# Revit family: Emeco - 1 Inch Stool - Seat Material - Color - Aluminum Frame Finish
name_source: partatom
category: Furniture
revit_build: Autodesk Revit MEP 2014 (Build: 20140709_2115(x64)
units: mm (PartAtom-declared; Revit-internal decimal feet)

## types (20) — shared parameters
Assembly Code = E2020200
Description = Stool
Glide Material = Emeco-Glide-Plastic-Grey
Manufacturer = Emeco
URL = https://www.emeco.net
Upholster Material = Emeco-Upholester-Fabric

## per-type parameters (varying)
| type | Chair Frame Material | Fabric Visibility | Plastic Visibility | Plywood Material | Plywood Visibility | Seat Material_Fabric | Seat Material_Plastic_Blue | Seat Material_Plastic_Bordeaux | Seat Material_Plastic_Brown | Seat Material_Plastic_Dark Grey | Seat Material_Plastic_Green | Seat Material_Plastic_Light Grey | Seat Material_Plastic_Ochre Red | Seat Material_Plywood_Ash | Seat Material_Plywood_Walnut | Seat Type Selector |
| Reclaimed Polypropylene - Blue - Black Frame | Emeco-Frame-Metal-Aluminum-Black Powder Coated | No | Yes | Emeco-Seat-Plywood-Walnut | No | No | Yes | No | No | No | No | No | No | No | No | 9 |
| Reclaimed Polypropylene - Blue - Brushed Frame | Emeco-Frame-Metal-Aluminium-Brushed | No | Yes | Emeco-Seat-Plywood-Walnut | No | No | Yes | No | No | No | No | No | No | No | No | 9 |
| Reclaimed Polypropylene - Bordeaux - Black Frame | Emeco-Frame-Metal-Aluminum-Black Powder Coated | No | Yes | Emeco-Seat-Plywood-Walnut | No | No | No | Yes | No | No | No | No | No | No | No | 8 |
| Reclaimed Polypropylene - Bordeaux - Brushed Frame | Emeco-Frame-Metal-Aluminium-Brushed | No | Yes | Emeco-Seat-Plywood-Walnut | No | No | No | Yes | No | No | No | No | No | No | No | 8 |
| Reclaimed Polypropylene - Brown - Black Frame | Emeco-Frame-Metal-Aluminum-Black Powder Coated | No | Yes | Emeco-Seat-Plywood-Walnut | No | No | No | No | Yes | No | No | No | No | No | No | 7 |
| Reclaimed Polypropylene - Brown - Brushed Frame | Emeco-Frame-Metal-Aluminium-Brushed | No | Yes | Emeco-Seat-Plywood-Walnut | No | No | No | No | Yes | No | No | No | No | No | No | 7 |
| Reclaimed Polypropylene - Dark Grey - Black Frame | Emeco-Frame-Metal-Aluminum-Black Powder Coated | No | Yes | Emeco-Seat-Plywood-Walnut | No | No | No | No | No | Yes | No | No | No | No | No | 6 |
| Reclaimed Polypropylene - Dark Grey - Brushed Frame | Emeco-Frame-Metal-Aluminium-Brushed | No | Yes | Emeco-Seat-Plywood-Walnut | No | No | No | No | No | Yes | No | No | No | No | No | 6 |
| Reclaimed Polypropylene - Green - Black Frame | Emeco-Frame-Metal-Aluminum-Black Powder Coated | No | Yes | Emeco-Seat-Plywood-Walnut | No | No | No | No | No | No | Yes | No | No | No | No | 5 |
| Reclaimed Polypropylene - Green - Brushed Frame | Emeco-Frame-Metal-Aluminium-Brushed | No | Yes | Emeco-Seat-Plywood-Walnut | No | No | No | No | No | No | Yes | No | No | No | No | 5 |
| Reclaimed Polypropylene - Light Grey - Black Frame | Emeco-Frame-Metal-Aluminum-Black Powder Coated | No | Yes | Emeco-Seat-Plywood-Walnut | No | No | No | No | No | No | No | Yes | No | No | No | 4 |
| Reclaimed Polypropylene - Light Grey - Brushed Frame | Emeco-Frame-Metal-Aluminium-Brushed | No | Yes | Emeco-Seat-Plywood-Walnut | No | No | No | No | No | No | No | Yes | No | No | No | 4 |
| Reclaimed Polypropylene - Ochre Red - Black Frame | Emeco-Frame-Metal-Aluminum-Black Powder Coated | No | Yes | Emeco-Seat-Plywood-Walnut | No | No | No | No | No | No | No | No | Yes | No | No | 3 |
| Reclaimed Polypropylene - Ochre Red - Brushed Frame | Emeco-Frame-Metal-Aluminium-Brushed | No | Yes | Emeco-Seat-Plywood-Walnut | No | No | No | No | No | No | No | No | Yes | No | No | 3 |
| Upholstered - Grey Fabric - Black Frame | Emeco-Frame-Metal-Aluminum-Black Powder Coated | Yes | No | Emeco-Seat-Plywood-Walnut | No | Yes | No | No | No | No | No | No | No | No | No | 0 |
| Upholstered - Grey Fabric - Brushed Frame | Emeco-Frame-Metal-Aluminium-Brushed | Yes | No | Emeco-Seat-Plywood-Walnut | No | Yes | No | No | No | No | No | No | No | No | No | 0 |
| Wood - Ash - Black Frame | Emeco-Frame-Metal-Aluminum-Black Powder Coated | No | No | Emeco-Seat-Plywood-Ash | Yes | No | No | No | No | No | No | No | No | Yes | No | 2 |
| Wood - Ash - Brushed Frame | Emeco-Frame-Metal-Aluminium-Brushed | No | No | Emeco-Seat-Plywood-Ash | Yes | No | No | No | No | No | No | No | No | Yes | No | 2 |
| Wood - Walnut - Black Frame | Emeco-Frame-Metal-Aluminum-Black Powder Coated | No | No | Emeco-Seat-Plywood-Walnut | Yes | No | No | No | No | No | No | No | No | No | Yes | 1 |
| Wood - Walnut - Brushed Frame | Emeco-Frame-Metal-Aluminium-Brushed | No | No | Emeco-Seat-Plywood-Walnut | Yes | No | No | No | No | No | No | No | No | No | Yes | 1 |

## geometry (parser evidence)
native form markers: Sweep x3
no freeform markers — native parametric forms only
